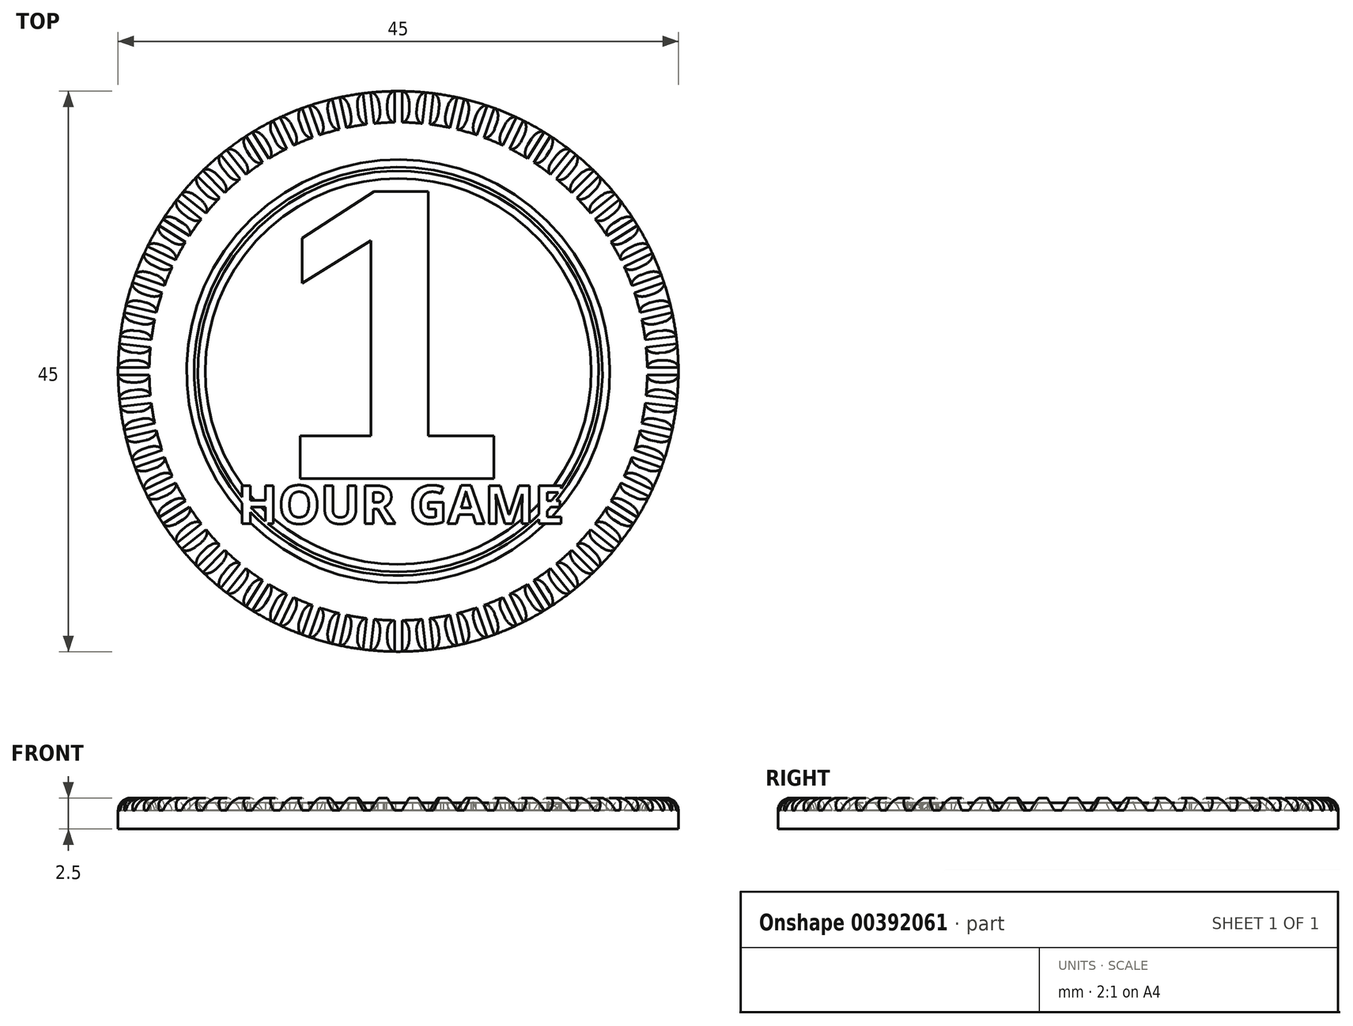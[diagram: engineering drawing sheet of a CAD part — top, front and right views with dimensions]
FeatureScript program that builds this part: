
annotation { "Feature Type Name" : "Feature", "Feature Type Description" : "" }
export const myFeature = defineFeature(function(context is Context, id is Id, definition is map)
    precondition{}
    {
        {
            var Q0;
            Q0=qCreatedBy(makeId("Top.planeOp"),FACE);
            var sketch = newSketch(context, id + "F0", { "sketchPlane" : qUnion([Q0])});
            skCircle(sketch, "E0", {"center": v(0, 0) * mm, "radius": 22.5 * mm});
            skSolve(sketch);
        }
        {
            var Q0;
            Q0 = qSketchRegion(id + "F0", true);
            extrude(context, id + "F1", {"entities" : qUnion([Q0]), "depth" : 2.5 * mm});
        }
        {
            var Q0;
            Q0=makeQuery(id+"F1.opExtrude","CAP_FACE",FACE,{"disambiguationData":[OSD([sQuery(id+"F0.wireOp",EDGE,"E0")])],"isStart":false});
            var sketch = newSketch(context, id + "F2", { "sketchPlane" : qUnion([Q0])});
            skCircle(sketch, "E1.0", {"center": v(0, 0) * mm, "radius": 20 * mm});
            skSolve(sketch);
        }
        {
            var Q0;
            Q0 = qSketchRegion(id + "F2", true);
            extrude(context, id + "F3", {"entities" : qUnion([Q0]), "operationType" : NewBodyOperationType.REMOVE, "oppositeDirection" : true, "depth" : 1 * mm});
        }
        {
            var Q0;
            Q0=makeQuery(id+"F1.opExtrude","CAP_FACE",FACE,{"disambiguationData":[OSD([sQuery(id+"F0.wireOp",EDGE,"E0")])],"isStart":false});
            fillet(context, id + "F4", {"entities" : qUnion([Q0]), "radius" : 1 * mm, "tangentPropagation" : true, "allowEdgeOverflow" : false});
        }
        {
            var Q0;
            Q0=qCreatedBy(makeId("Right.planeOp"),FACE);
            var sketch = newSketch(context, id + "F5", { "sketchPlane" : qUnion([Q0])});
            skLineSegment(sketch, "E2", {"start": v(0, 0) * mm, "end": v(0, 4.13) * mm, "construction": true});
            skLineSegment(sketch, "E3", {"start": v(0, 1.5) * mm, "end": v(-0.3, 1.5) * mm});
            skLineSegment(sketch, "E4", {"start": v(-0.3, 1.5) * mm, "end": v(-0.88, 2.5) * mm});
            skLineSegment(sketch, "E5", {"start": v(-0.88, 2.5) * mm, "end": v(0, 2.5) * mm});
            skLineSegment(sketch, "E6.MirrorCS", {"start": v(0, 1.5) * mm, "end": v(0.3, 1.5) * mm});
            skLineSegment(sketch, "E7.MirrorCS", {"start": v(0.88, 2.5) * mm, "end": v(0, 2.5) * mm});
            skLineSegment(sketch, "E8.MirrorCS", {"start": v(0.3, 1.5) * mm, "end": v(0.88, 2.5) * mm});
            skSolve(sketch);
        }
        {
            var Q0;
            Q0 = qSketchRegion(id + "F5", true);
            extrude(context, id + "F6", {"entities" : qUnion([Q0]), "endBound" : BoundingType.THROUGH_ALL, "oppositeDirection" : true, "depth" : 25 * mm});
        }
        {
            var Q0;
            Q0=qCreatedBy(makeId("Front.planeOp"),FACE);
            var sketch = newSketch(context, id + "F7", { "sketchPlane" : qUnion([Q0])});
            skLineSegment(sketch, "E9", {"start": v(0, 0) * mm, "end": v(0, 9.54) * mm});
            skSolve(sketch);
        }
        {
            var Q0;
            Q0=makeQuery(id+"F6.opExtrude","SWEPT_BODY",BODY,{"disambiguationData":[OSD([sQuery(id+"F5.wireOp",EDGE,"E3"),sQuery(id+"F5.wireOp",EDGE,"E4"),sQuery(id+"F5.wireOp",EDGE,"E5"),sQuery(id+"F5.wireOp",EDGE,"E6.MirrorCS"),sQuery(id+"F5.wireOp",EDGE,"E7.MirrorCS"),sQuery(id+"F5.wireOp",EDGE,"E8.MirrorCS")])]});
            var Q1;
            Q1=sQuery(id+"F7.wireOp",EDGE,"E9");
            circularPattern(context, id + "F8", {"operationType" : NewBodyOperationType.REMOVE, "entities" : qUnion([Q0]), "axis" : qUnion([Q1]), "angle" : 360 * degree, "instanceCount" : 56, "equalSpace" : true, "computeTransformsWithoutBuiltin" : true});
        }
        {
            var Q0;
            {var subQ0=makeQuery(id+"F6.opExtrude","SWEPT_FACE",FACE,{"disambiguationData":[OSD([sQuery(id+"F5.wireOp",EDGE,"E3"),sQuery(id+"F5.wireOp",EDGE,"E6.MirrorCS")])]});Q0=makeQuery(id+"F8.boolean.opBoolean","MERGE",FACE,{"derivedFrom":[makeQuery(id+"F3.boolean.opBoolean","COPY",FACE,{"derivedFrom":makeQuery(id+"F3.opExtrude","CAP_FACE",FACE,{"disambiguationData":[OSD([sQuery(id+"F2.wireOp",EDGE,"E1.0")])],"isStart":false})}),subQ0,makeQuery(id+"F8.opPattern","COPY",FACE,{"derivedFrom":subQ0,"instanceName":"1"}),makeQuery(id+"F8.opPattern","COPY",FACE,{"derivedFrom":subQ0,"instanceName":"2"}),makeQuery(id+"F8.opPattern","COPY",FACE,{"derivedFrom":subQ0,"instanceName":"3"}),makeQuery(id+"F8.opPattern","COPY",FACE,{"derivedFrom":subQ0,"instanceName":"4"}),makeQuery(id+"F8.opPattern","COPY",FACE,{"derivedFrom":subQ0,"instanceName":"5"}),makeQuery(id+"F8.opPattern","COPY",FACE,{"derivedFrom":subQ0,"instanceName":"6"}),makeQuery(id+"F8.opPattern","COPY",FACE,{"derivedFrom":subQ0,"instanceName":"7"}),makeQuery(id+"F8.opPattern","COPY",FACE,{"derivedFrom":subQ0,"instanceName":"8"}),makeQuery(id+"F8.opPattern","COPY",FACE,{"derivedFrom":subQ0,"instanceName":"9"}),makeQuery(id+"F8.opPattern","COPY",FACE,{"derivedFrom":subQ0,"instanceName":"10"}),makeQuery(id+"F8.opPattern","COPY",FACE,{"derivedFrom":subQ0,"instanceName":"11"}),makeQuery(id+"F8.opPattern","COPY",FACE,{"derivedFrom":subQ0,"instanceName":"12"}),makeQuery(id+"F8.opPattern","COPY",FACE,{"derivedFrom":subQ0,"instanceName":"13"}),makeQuery(id+"F8.opPattern","COPY",FACE,{"derivedFrom":subQ0,"instanceName":"14"}),makeQuery(id+"F8.opPattern","COPY",FACE,{"derivedFrom":subQ0,"instanceName":"15"}),makeQuery(id+"F8.opPattern","COPY",FACE,{"derivedFrom":subQ0,"instanceName":"16"}),makeQuery(id+"F8.opPattern","COPY",FACE,{"derivedFrom":subQ0,"instanceName":"17"}),makeQuery(id+"F8.opPattern","COPY",FACE,{"derivedFrom":subQ0,"instanceName":"18"}),makeQuery(id+"F8.opPattern","COPY",FACE,{"derivedFrom":subQ0,"instanceName":"19"}),makeQuery(id+"F8.opPattern","COPY",FACE,{"derivedFrom":subQ0,"instanceName":"20"}),makeQuery(id+"F8.opPattern","COPY",FACE,{"derivedFrom":subQ0,"instanceName":"21"}),makeQuery(id+"F8.opPattern","COPY",FACE,{"derivedFrom":subQ0,"instanceName":"22"}),makeQuery(id+"F8.opPattern","COPY",FACE,{"derivedFrom":subQ0,"instanceName":"23"}),makeQuery(id+"F8.opPattern","COPY",FACE,{"derivedFrom":subQ0,"instanceName":"24"}),makeQuery(id+"F8.opPattern","COPY",FACE,{"derivedFrom":subQ0,"instanceName":"25"}),makeQuery(id+"F8.opPattern","COPY",FACE,{"derivedFrom":subQ0,"instanceName":"26"}),makeQuery(id+"F8.opPattern","COPY",FACE,{"derivedFrom":subQ0,"instanceName":"27"}),makeQuery(id+"F8.opPattern","COPY",FACE,{"derivedFrom":subQ0,"instanceName":"28"}),makeQuery(id+"F8.opPattern","COPY",FACE,{"derivedFrom":subQ0,"instanceName":"29"}),makeQuery(id+"F8.opPattern","COPY",FACE,{"derivedFrom":subQ0,"instanceName":"30"}),makeQuery(id+"F8.opPattern","COPY",FACE,{"derivedFrom":subQ0,"instanceName":"31"}),makeQuery(id+"F8.opPattern","COPY",FACE,{"derivedFrom":subQ0,"instanceName":"32"}),makeQuery(id+"F8.opPattern","COPY",FACE,{"derivedFrom":subQ0,"instanceName":"33"}),makeQuery(id+"F8.opPattern","COPY",FACE,{"derivedFrom":subQ0,"instanceName":"34"}),makeQuery(id+"F8.opPattern","COPY",FACE,{"derivedFrom":subQ0,"instanceName":"35"}),makeQuery(id+"F8.opPattern","COPY",FACE,{"derivedFrom":subQ0,"instanceName":"36"}),makeQuery(id+"F8.opPattern","COPY",FACE,{"derivedFrom":subQ0,"instanceName":"37"}),makeQuery(id+"F8.opPattern","COPY",FACE,{"derivedFrom":subQ0,"instanceName":"38"}),makeQuery(id+"F8.opPattern","COPY",FACE,{"derivedFrom":subQ0,"instanceName":"39"}),makeQuery(id+"F8.opPattern","COPY",FACE,{"derivedFrom":subQ0,"instanceName":"40"}),makeQuery(id+"F8.opPattern","COPY",FACE,{"derivedFrom":subQ0,"instanceName":"41"}),makeQuery(id+"F8.opPattern","COPY",FACE,{"derivedFrom":subQ0,"instanceName":"42"}),makeQuery(id+"F8.opPattern","COPY",FACE,{"derivedFrom":subQ0,"instanceName":"43"}),makeQuery(id+"F8.opPattern","COPY",FACE,{"derivedFrom":subQ0,"instanceName":"44"}),makeQuery(id+"F8.opPattern","COPY",FACE,{"derivedFrom":subQ0,"instanceName":"45"}),makeQuery(id+"F8.opPattern","COPY",FACE,{"derivedFrom":subQ0,"instanceName":"46"}),makeQuery(id+"F8.opPattern","COPY",FACE,{"derivedFrom":subQ0,"instanceName":"47"}),makeQuery(id+"F8.opPattern","COPY",FACE,{"derivedFrom":subQ0,"instanceName":"48"}),makeQuery(id+"F8.opPattern","COPY",FACE,{"derivedFrom":subQ0,"instanceName":"49"}),makeQuery(id+"F8.opPattern","COPY",FACE,{"derivedFrom":subQ0,"instanceName":"50"}),makeQuery(id+"F8.opPattern","COPY",FACE,{"derivedFrom":subQ0,"instanceName":"51"}),makeQuery(id+"F8.opPattern","COPY",FACE,{"derivedFrom":subQ0,"instanceName":"52"}),makeQuery(id+"F8.opPattern","COPY",FACE,{"derivedFrom":subQ0,"instanceName":"53"}),makeQuery(id+"F8.opPattern","COPY",FACE,{"derivedFrom":subQ0,"instanceName":"54"}),makeQuery(id+"F8.opPattern","COPY",FACE,{"derivedFrom":subQ0,"instanceName":"55"})]});}
            var sketch = newSketch(context, id + "F9", { "sketchPlane" : qUnion([Q0])});
            skText(sketch, "E10", { "text": "1", "fontName": "Arimo-Bold.ttf"});
            const initialGuessF9  = {"E10": [-0.01, -0.0086, 1, 0, 0.0241]};
            skSetInitialGuess(sketch, initialGuessF9);
            skSolve(sketch);
        }
        {
            var Q0;
            Q0 = qSketchRegion(id + "F9", true);
            extrude(context, id + "F10", {"entities" : qUnion([Q0]), "operationType" : NewBodyOperationType.ADD, "depth" : 0.6 * mm});
        }
        {
            var Q0;
            {var subQ0=makeQuery(id+"F6.opExtrude","SWEPT_FACE",FACE,{"disambiguationData":[OSD([sQuery(id+"F5.wireOp",EDGE,"E3"),sQuery(id+"F5.wireOp",EDGE,"E6.MirrorCS")])]});Q0=makeQuery(id+"F8.boolean.opBoolean","MERGE",FACE,{"derivedFrom":[makeQuery(id+"F3.boolean.opBoolean","COPY",FACE,{"derivedFrom":makeQuery(id+"F3.opExtrude","CAP_FACE",FACE,{"disambiguationData":[OSD([sQuery(id+"F2.wireOp",EDGE,"E1.0")])],"isStart":false})}),subQ0,makeQuery(id+"F8.opPattern","COPY",FACE,{"derivedFrom":subQ0,"instanceName":"1"}),makeQuery(id+"F8.opPattern","COPY",FACE,{"derivedFrom":subQ0,"instanceName":"2"}),makeQuery(id+"F8.opPattern","COPY",FACE,{"derivedFrom":subQ0,"instanceName":"3"}),makeQuery(id+"F8.opPattern","COPY",FACE,{"derivedFrom":subQ0,"instanceName":"4"}),makeQuery(id+"F8.opPattern","COPY",FACE,{"derivedFrom":subQ0,"instanceName":"5"}),makeQuery(id+"F8.opPattern","COPY",FACE,{"derivedFrom":subQ0,"instanceName":"6"}),makeQuery(id+"F8.opPattern","COPY",FACE,{"derivedFrom":subQ0,"instanceName":"7"}),makeQuery(id+"F8.opPattern","COPY",FACE,{"derivedFrom":subQ0,"instanceName":"8"}),makeQuery(id+"F8.opPattern","COPY",FACE,{"derivedFrom":subQ0,"instanceName":"9"}),makeQuery(id+"F8.opPattern","COPY",FACE,{"derivedFrom":subQ0,"instanceName":"10"}),makeQuery(id+"F8.opPattern","COPY",FACE,{"derivedFrom":subQ0,"instanceName":"11"}),makeQuery(id+"F8.opPattern","COPY",FACE,{"derivedFrom":subQ0,"instanceName":"12"}),makeQuery(id+"F8.opPattern","COPY",FACE,{"derivedFrom":subQ0,"instanceName":"13"}),makeQuery(id+"F8.opPattern","COPY",FACE,{"derivedFrom":subQ0,"instanceName":"14"}),makeQuery(id+"F8.opPattern","COPY",FACE,{"derivedFrom":subQ0,"instanceName":"15"}),makeQuery(id+"F8.opPattern","COPY",FACE,{"derivedFrom":subQ0,"instanceName":"16"}),makeQuery(id+"F8.opPattern","COPY",FACE,{"derivedFrom":subQ0,"instanceName":"17"}),makeQuery(id+"F8.opPattern","COPY",FACE,{"derivedFrom":subQ0,"instanceName":"18"}),makeQuery(id+"F8.opPattern","COPY",FACE,{"derivedFrom":subQ0,"instanceName":"19"}),makeQuery(id+"F8.opPattern","COPY",FACE,{"derivedFrom":subQ0,"instanceName":"20"}),makeQuery(id+"F8.opPattern","COPY",FACE,{"derivedFrom":subQ0,"instanceName":"21"}),makeQuery(id+"F8.opPattern","COPY",FACE,{"derivedFrom":subQ0,"instanceName":"22"}),makeQuery(id+"F8.opPattern","COPY",FACE,{"derivedFrom":subQ0,"instanceName":"23"}),makeQuery(id+"F8.opPattern","COPY",FACE,{"derivedFrom":subQ0,"instanceName":"24"}),makeQuery(id+"F8.opPattern","COPY",FACE,{"derivedFrom":subQ0,"instanceName":"25"}),makeQuery(id+"F8.opPattern","COPY",FACE,{"derivedFrom":subQ0,"instanceName":"26"}),makeQuery(id+"F8.opPattern","COPY",FACE,{"derivedFrom":subQ0,"instanceName":"27"}),makeQuery(id+"F8.opPattern","COPY",FACE,{"derivedFrom":subQ0,"instanceName":"28"}),makeQuery(id+"F8.opPattern","COPY",FACE,{"derivedFrom":subQ0,"instanceName":"29"}),makeQuery(id+"F8.opPattern","COPY",FACE,{"derivedFrom":subQ0,"instanceName":"30"}),makeQuery(id+"F8.opPattern","COPY",FACE,{"derivedFrom":subQ0,"instanceName":"31"}),makeQuery(id+"F8.opPattern","COPY",FACE,{"derivedFrom":subQ0,"instanceName":"32"}),makeQuery(id+"F8.opPattern","COPY",FACE,{"derivedFrom":subQ0,"instanceName":"33"}),makeQuery(id+"F8.opPattern","COPY",FACE,{"derivedFrom":subQ0,"instanceName":"34"}),makeQuery(id+"F8.opPattern","COPY",FACE,{"derivedFrom":subQ0,"instanceName":"35"}),makeQuery(id+"F8.opPattern","COPY",FACE,{"derivedFrom":subQ0,"instanceName":"36"}),makeQuery(id+"F8.opPattern","COPY",FACE,{"derivedFrom":subQ0,"instanceName":"37"}),makeQuery(id+"F8.opPattern","COPY",FACE,{"derivedFrom":subQ0,"instanceName":"38"}),makeQuery(id+"F8.opPattern","COPY",FACE,{"derivedFrom":subQ0,"instanceName":"39"}),makeQuery(id+"F8.opPattern","COPY",FACE,{"derivedFrom":subQ0,"instanceName":"40"}),makeQuery(id+"F8.opPattern","COPY",FACE,{"derivedFrom":subQ0,"instanceName":"41"}),makeQuery(id+"F8.opPattern","COPY",FACE,{"derivedFrom":subQ0,"instanceName":"42"}),makeQuery(id+"F8.opPattern","COPY",FACE,{"derivedFrom":subQ0,"instanceName":"43"}),makeQuery(id+"F8.opPattern","COPY",FACE,{"derivedFrom":subQ0,"instanceName":"44"}),makeQuery(id+"F8.opPattern","COPY",FACE,{"derivedFrom":subQ0,"instanceName":"45"}),makeQuery(id+"F8.opPattern","COPY",FACE,{"derivedFrom":subQ0,"instanceName":"46"}),makeQuery(id+"F8.opPattern","COPY",FACE,{"derivedFrom":subQ0,"instanceName":"47"}),makeQuery(id+"F8.opPattern","COPY",FACE,{"derivedFrom":subQ0,"instanceName":"48"}),makeQuery(id+"F8.opPattern","COPY",FACE,{"derivedFrom":subQ0,"instanceName":"49"}),makeQuery(id+"F8.opPattern","COPY",FACE,{"derivedFrom":subQ0,"instanceName":"50"}),makeQuery(id+"F8.opPattern","COPY",FACE,{"derivedFrom":subQ0,"instanceName":"51"}),makeQuery(id+"F8.opPattern","COPY",FACE,{"derivedFrom":subQ0,"instanceName":"52"}),makeQuery(id+"F8.opPattern","COPY",FACE,{"derivedFrom":subQ0,"instanceName":"53"}),makeQuery(id+"F8.opPattern","COPY",FACE,{"derivedFrom":subQ0,"instanceName":"54"}),makeQuery(id+"F8.opPattern","COPY",FACE,{"derivedFrom":subQ0,"instanceName":"55"})]});}
            var sketch = newSketch(context, id + "F11", { "sketchPlane" : qUnion([Q0])});
            skText(sketch, "E11", { "text": "HOUR GAME", "fontName": "OpenSans-Bold.ttf"});
            const initialGuessF11  = {"E11": [-0.01292, -0.01222, 1, 0, 0.00307]};
            skSetInitialGuess(sketch, initialGuessF11);
            skSolve(sketch);
        }
        {
            var Q0;
            Q0 = qSketchRegion(id + "F11", true);
            extrude(context, id + "F12", {"entities" : qUnion([Q0]), "operationType" : NewBodyOperationType.ADD, "depth" : 0.6 * mm});
        }
        {
            var Q0;
            {var subQ2=sQuery(id+"F0.wireOp",EDGE,"E0");var subQ3=sQuery(id+"F2.wireOp",EDGE,"E1.0");var subQ4=makeQuery(id+"F6.opExtrude","SWEPT_FACE",FACE,{"disambiguationData":[OSD([sQuery(id+"F5.wireOp",EDGE,"E3"),sQuery(id+"F5.wireOp",EDGE,"E6.MirrorCS")])]});Q0=makeQuery(id+"F12.boolean.opBoolean","SPLIT",FACE,{"disambiguationData":[TD([makeQuery(id+"F1.opExtrude","SWEPT_FACE",FACE,{"disambiguationData":[OSD([subQ2])]})])],"derivedFrom":makeQuery(id+"F8.boolean.opBoolean","MERGE",FACE,{"derivedFrom":[makeQuery(id+"F3.boolean.opBoolean","COPY",FACE,{"derivedFrom":makeQuery(id+"F3.opExtrude","CAP_FACE",FACE,{"disambiguationData":[OSD([subQ3])],"isStart":false})}),subQ4,makeQuery(id+"F8.opPattern","COPY",FACE,{"derivedFrom":subQ4,"instanceName":"1"}),makeQuery(id+"F8.opPattern","COPY",FACE,{"derivedFrom":subQ4,"instanceName":"2"}),makeQuery(id+"F8.opPattern","COPY",FACE,{"derivedFrom":subQ4,"instanceName":"3"}),makeQuery(id+"F8.opPattern","COPY",FACE,{"derivedFrom":subQ4,"instanceName":"4"}),makeQuery(id+"F8.opPattern","COPY",FACE,{"derivedFrom":subQ4,"instanceName":"5"}),makeQuery(id+"F8.opPattern","COPY",FACE,{"derivedFrom":subQ4,"instanceName":"6"}),makeQuery(id+"F8.opPattern","COPY",FACE,{"derivedFrom":subQ4,"instanceName":"7"}),makeQuery(id+"F8.opPattern","COPY",FACE,{"derivedFrom":subQ4,"instanceName":"8"}),makeQuery(id+"F8.opPattern","COPY",FACE,{"derivedFrom":subQ4,"instanceName":"9"}),makeQuery(id+"F8.opPattern","COPY",FACE,{"derivedFrom":subQ4,"instanceName":"10"}),makeQuery(id+"F8.opPattern","COPY",FACE,{"derivedFrom":subQ4,"instanceName":"11"}),makeQuery(id+"F8.opPattern","COPY",FACE,{"derivedFrom":subQ4,"instanceName":"12"}),makeQuery(id+"F8.opPattern","COPY",FACE,{"derivedFrom":subQ4,"instanceName":"13"}),makeQuery(id+"F8.opPattern","COPY",FACE,{"derivedFrom":subQ4,"instanceName":"14"}),makeQuery(id+"F8.opPattern","COPY",FACE,{"derivedFrom":subQ4,"instanceName":"15"}),makeQuery(id+"F8.opPattern","COPY",FACE,{"derivedFrom":subQ4,"instanceName":"16"}),makeQuery(id+"F8.opPattern","COPY",FACE,{"derivedFrom":subQ4,"instanceName":"17"}),makeQuery(id+"F8.opPattern","COPY",FACE,{"derivedFrom":subQ4,"instanceName":"18"}),makeQuery(id+"F8.opPattern","COPY",FACE,{"derivedFrom":subQ4,"instanceName":"19"}),makeQuery(id+"F8.opPattern","COPY",FACE,{"derivedFrom":subQ4,"instanceName":"20"}),makeQuery(id+"F8.opPattern","COPY",FACE,{"derivedFrom":subQ4,"instanceName":"21"}),makeQuery(id+"F8.opPattern","COPY",FACE,{"derivedFrom":subQ4,"instanceName":"22"}),makeQuery(id+"F8.opPattern","COPY",FACE,{"derivedFrom":subQ4,"instanceName":"23"}),makeQuery(id+"F8.opPattern","COPY",FACE,{"derivedFrom":subQ4,"instanceName":"24"}),makeQuery(id+"F8.opPattern","COPY",FACE,{"derivedFrom":subQ4,"instanceName":"25"}),makeQuery(id+"F8.opPattern","COPY",FACE,{"derivedFrom":subQ4,"instanceName":"26"}),makeQuery(id+"F8.opPattern","COPY",FACE,{"derivedFrom":subQ4,"instanceName":"27"}),makeQuery(id+"F8.opPattern","COPY",FACE,{"derivedFrom":subQ4,"instanceName":"28"}),makeQuery(id+"F8.opPattern","COPY",FACE,{"derivedFrom":subQ4,"instanceName":"29"}),makeQuery(id+"F8.opPattern","COPY",FACE,{"derivedFrom":subQ4,"instanceName":"30"}),makeQuery(id+"F8.opPattern","COPY",FACE,{"derivedFrom":subQ4,"instanceName":"31"}),makeQuery(id+"F8.opPattern","COPY",FACE,{"derivedFrom":subQ4,"instanceName":"32"}),makeQuery(id+"F8.opPattern","COPY",FACE,{"derivedFrom":subQ4,"instanceName":"33"}),makeQuery(id+"F8.opPattern","COPY",FACE,{"derivedFrom":subQ4,"instanceName":"34"}),makeQuery(id+"F8.opPattern","COPY",FACE,{"derivedFrom":subQ4,"instanceName":"35"}),makeQuery(id+"F8.opPattern","COPY",FACE,{"derivedFrom":subQ4,"instanceName":"36"}),makeQuery(id+"F8.opPattern","COPY",FACE,{"derivedFrom":subQ4,"instanceName":"37"}),makeQuery(id+"F8.opPattern","COPY",FACE,{"derivedFrom":subQ4,"instanceName":"38"}),makeQuery(id+"F8.opPattern","COPY",FACE,{"derivedFrom":subQ4,"instanceName":"39"}),makeQuery(id+"F8.opPattern","COPY",FACE,{"derivedFrom":subQ4,"instanceName":"40"}),makeQuery(id+"F8.opPattern","COPY",FACE,{"derivedFrom":subQ4,"instanceName":"41"}),makeQuery(id+"F8.opPattern","COPY",FACE,{"derivedFrom":subQ4,"instanceName":"42"}),makeQuery(id+"F8.opPattern","COPY",FACE,{"derivedFrom":subQ4,"instanceName":"43"}),makeQuery(id+"F8.opPattern","COPY",FACE,{"derivedFrom":subQ4,"instanceName":"44"}),makeQuery(id+"F8.opPattern","COPY",FACE,{"derivedFrom":subQ4,"instanceName":"45"}),makeQuery(id+"F8.opPattern","COPY",FACE,{"derivedFrom":subQ4,"instanceName":"46"}),makeQuery(id+"F8.opPattern","COPY",FACE,{"derivedFrom":subQ4,"instanceName":"47"}),makeQuery(id+"F8.opPattern","COPY",FACE,{"derivedFrom":subQ4,"instanceName":"48"}),makeQuery(id+"F8.opPattern","COPY",FACE,{"derivedFrom":subQ4,"instanceName":"49"}),makeQuery(id+"F8.opPattern","COPY",FACE,{"derivedFrom":subQ4,"instanceName":"50"}),makeQuery(id+"F8.opPattern","COPY",FACE,{"derivedFrom":subQ4,"instanceName":"51"}),makeQuery(id+"F8.opPattern","COPY",FACE,{"derivedFrom":subQ4,"instanceName":"52"}),makeQuery(id+"F8.opPattern","COPY",FACE,{"derivedFrom":subQ4,"instanceName":"53"}),makeQuery(id+"F8.opPattern","COPY",FACE,{"derivedFrom":subQ4,"instanceName":"54"}),makeQuery(id+"F8.opPattern","COPY",FACE,{"derivedFrom":subQ4,"instanceName":"55"})]})});}
            var sketch = newSketch(context, id + "F13", { "sketchPlane" : qUnion([Q0])});
            skCircle(sketch, "E12", {"center": v(0, 0) * mm, "radius": 15.5 * mm});
            skCircle(sketch, "E13.0", {"center": v(0, 0) * mm, "radius": 17 * mm});
            skSolve(sketch);
        }
        {
            var Q0;
            Q0 = qSketchRegion(id + "F13", true);
            extrude(context, id + "F14", {"entities" : qUnion([Q0]), "operationType" : NewBodyOperationType.ADD, "depth" : 0.6 * mm, "hasDraft" : true, "draftAngle" : 45 * degree, "draftPullDirection" : true});
        }
    });
